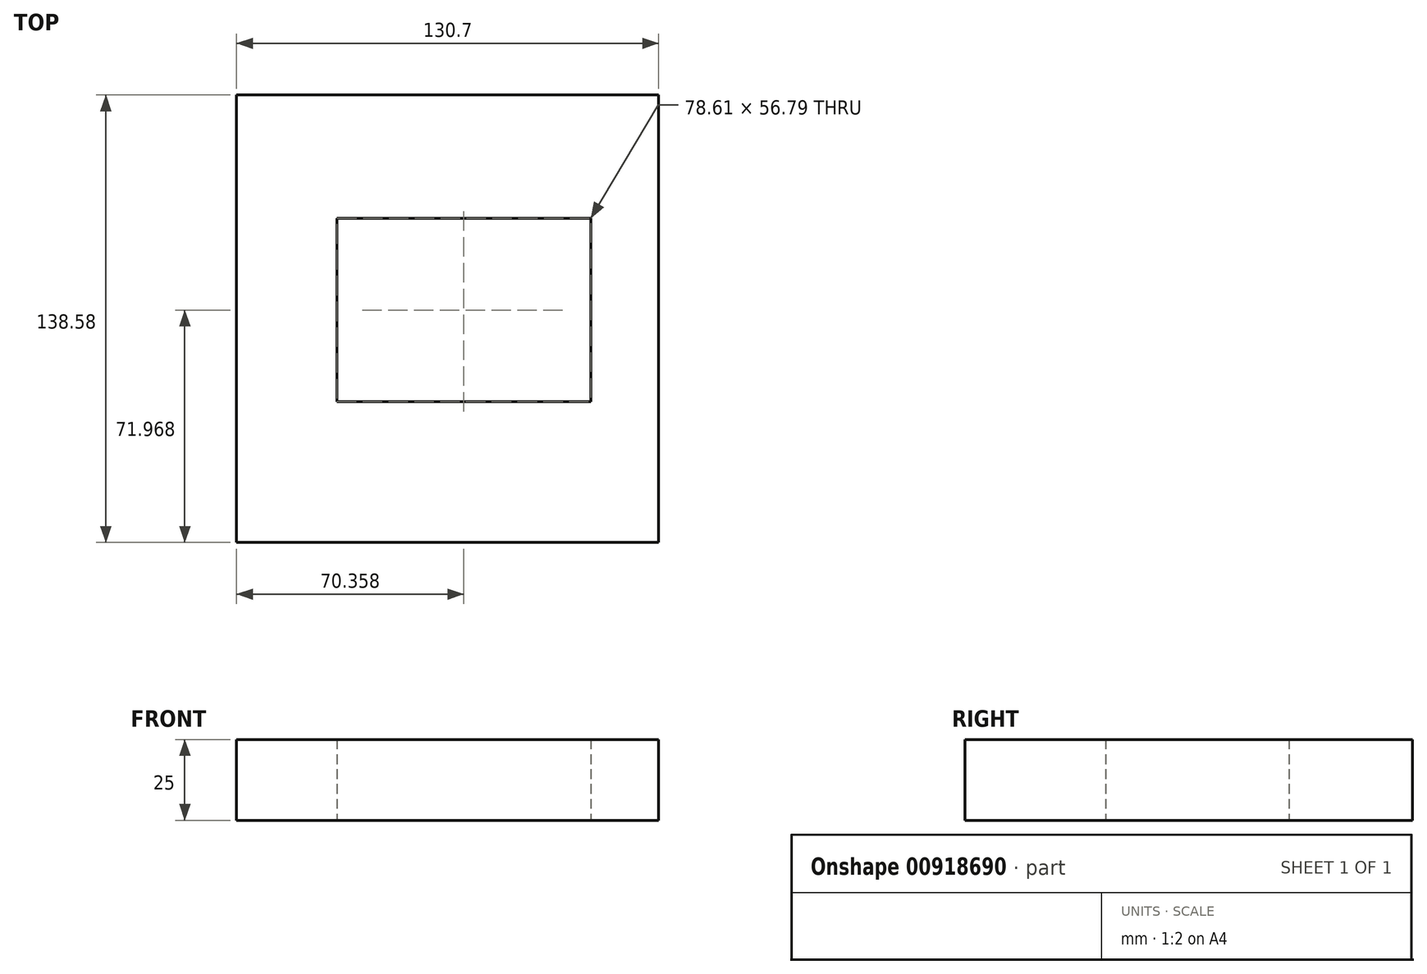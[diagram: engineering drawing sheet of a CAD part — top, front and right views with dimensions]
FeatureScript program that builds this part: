
annotation { "Feature Type Name" : "Feature", "Feature Type Description" : "" }
export const myFeature = defineFeature(function(context is Context, id is Id, definition is map)
    precondition{}
    {
        {
            var Q0;
            Q0=qCreatedBy(makeId("Top.planeOp"),FACE);
            var sketch = newSketch(context, id + "F0", { "sketchPlane" : qUnion([Q0])});
            skLineSegment(sketch, "E0.bottom", {"start": v(-65.35, -69.29) * mm, "end": v(65.35, -69.29) * mm});
            skLineSegment(sketch, "E0.top", {"start": v(-65.35, 69.29) * mm, "end": v(65.35, 69.29) * mm});
            skLineSegment(sketch, "E0.left", {"start": v(-65.35, -69.29) * mm, "end": v(-65.35, 69.29) * mm});
            skLineSegment(sketch, "E0.right", {"start": v(65.35, -69.29) * mm, "end": v(65.35, 69.29) * mm});
            skPoint(sketch, "E0.middle", {"position": v(0, 0) * mm});
            skLineSegment(sketch, "E1.bottom", {"start": v(-34.3, 31.07) * mm, "end": v(44.31, 31.07) * mm});
            skLineSegment(sketch, "E1.top", {"start": v(-34.3, -25.72) * mm, "end": v(44.31, -25.72) * mm});
            skLineSegment(sketch, "E1.left", {"start": v(-34.3, 31.07) * mm, "end": v(-34.3, -25.72) * mm});
            skLineSegment(sketch, "E1.right", {"start": v(44.31, 31.07) * mm, "end": v(44.31, -25.72) * mm});
            skSolve(sketch);
        }
        {
            var Q0;
            Q0=makeQuery(id+"F0.imprint","IMPRINT",FACE,{"disambiguationData":[TD([[makeQuery(id+"F0.imprint","IMPRINT",EDGE,{"derivedFrom":sQuery(id+"F0.wireOp",EDGE,"E0.bottom")}),1.0]])]});
            extrude(context, id + "F1", {"entities" : qUnion([Q0]), "depth" : 25 * mm, "offsetDistance" : 25 * mm});
        }
    });
